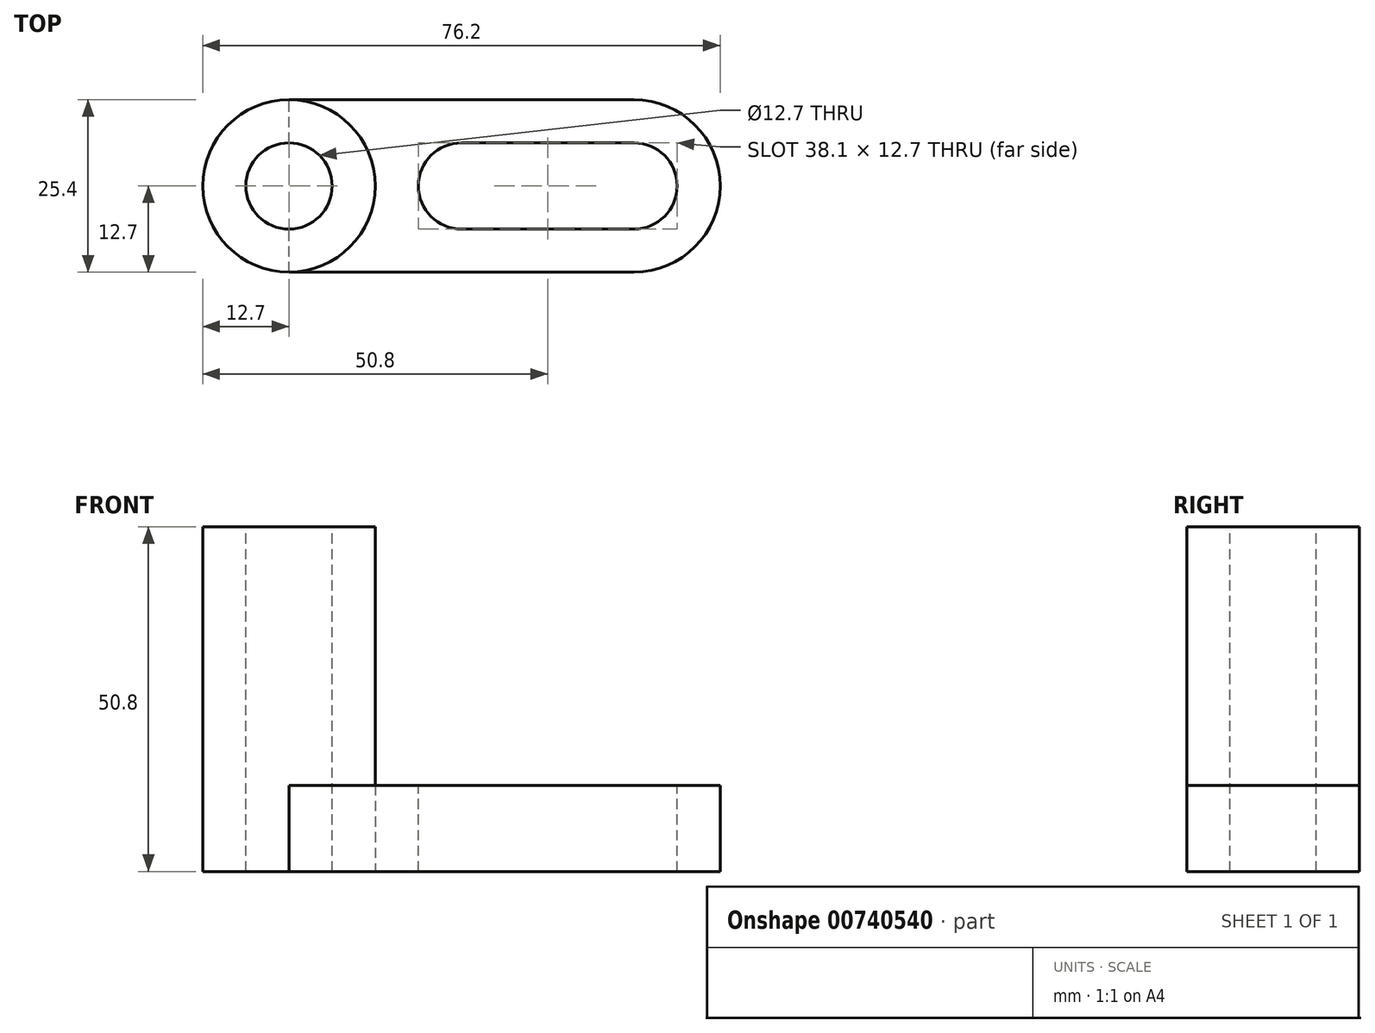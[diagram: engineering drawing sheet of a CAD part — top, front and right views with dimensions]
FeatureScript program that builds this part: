
annotation { "Feature Type Name" : "Feature", "Feature Type Description" : "" }
export const myFeature = defineFeature(function(context is Context, id is Id, definition is map)
    precondition{}
    {
        {
            var Q0;
            Q0=qCreatedBy(makeId("Top.planeOp"),FACE);
            var sketch = newSketch(context, id + "F0", { "sketchPlane" : qUnion([Q0])});
            skCircle(sketch, "E0", {"center": v(0, 0) * mm, "radius": 12.7 * mm});
            skSolve(sketch);
        }
        {
            var Q0;
            Q0=makeQuery(id+"F0.imprint","IMPRINT",FACE,{"disambiguationData":[TD([[makeQuery(id+"F0.imprint","IMPRINT",EDGE,{"derivedFrom":sQuery(id+"F0.wireOp",EDGE,"E0")}),1.0]])]});
            extrude(context, id + "F1", {"entities" : qUnion([Q0]), "depth" : 50.8 * mm, "offsetDistance" : 25.4 * mm});
        }
        {
            var Q0;
            Q0=qCreatedBy(makeId("Top.planeOp"),FACE);
            var sketch = newSketch(context, id + "F2", { "sketchPlane" : qUnion([Q0])});
            skLineSegment(sketch, "E1.bottom", {"start": v(0, -12.7) * mm, "end": v(50.8, -12.7) * mm});
            skLineSegment(sketch, "E1.top", {"start": v(0, 12.7) * mm, "end": v(50.8, 12.7) * mm});
            skLineSegment(sketch, "E1.left", {"start": v(0, -12.7) * mm, "end": v(0, 12.7) * mm});
            skLineSegment(sketch, "E1.right", {"start": v(50.8, -12.7) * mm, "end": v(50.8, 12.7) * mm});
            skCircle(sketch, "E2", {"center": v(50.8, 0) * mm, "radius": 12.7 * mm});
            skSolve(sketch);
        }
        {
            var Q0;
            Q0=makeQuery(id+"F2.imprint","IMPRINT",FACE,{"disambiguationData":[TD([[makeQuery(id+"F2.imprint","IMPRINT",EDGE,{"derivedFrom":sQuery(id+"F2.wireOp",EDGE,"E1.bottom")}),1.0]])]});
            var Q1;
            {var subQ0=sQuery(id+"F2.wireOp",EDGE,"E1.right");Q1=makeQuery(id+"F2.imprint","IMPRINT",FACE,{"disambiguationData":[TD([[makeQuery(id+"F2.imprint","IMPRINT",EDGE,{"derivedFrom":subQ0}),-1.0]])]});}
            var Q2;
            {var subQ0=sQuery(id+"F2.wireOp",EDGE,"E1.right");Q2=makeQuery(id+"F2.imprint","IMPRINT",FACE,{"disambiguationData":[TD([[makeQuery(id+"F2.imprint","IMPRINT",EDGE,{"derivedFrom":subQ0}),1.0]])]});}
            extrude(context, id + "F3", {"entities" : qUnion([Q0, Q1, Q2]), "depth" : 12.7 * mm, "offsetDistance" : 25.4 * mm});
        }
        {
            var Q0;
            Q0=makeQuery(id+"F3.opExtrude","CAP_FACE",FACE,{"disambiguationData":[OSD([sQuery(id+"F2.wireOp",EDGE,"E1.bottom"),sQuery(id+"F2.wireOp",EDGE,"E1.top"),sQuery(id+"F2.wireOp",EDGE,"E1.left"),sQuery(id+"F2.wireOp",EDGE,"E2")])],"isStart":false});
            var sketch = newSketch(context, id + "F4", { "sketchPlane" : qUnion([Q0])});
            skLineSegment(sketch, "E3.bottom", {"start": v(50.8, 6.35) * mm, "end": v(25.4, 6.35) * mm});
            skLineSegment(sketch, "E3.top", {"start": v(50.8, -6.35) * mm, "end": v(25.4, -6.35) * mm});
            skLineSegment(sketch, "E3.left", {"start": v(50.8, 6.35) * mm, "end": v(50.8, -6.35) * mm});
            skLineSegment(sketch, "E3.right", {"start": v(25.4, 6.35) * mm, "end": v(25.4, -6.35) * mm});
            skCircle(sketch, "E4", {"center": v(50.8, 0) * mm, "radius": 6.35 * mm});
            skCircle(sketch, "E5", {"center": v(25.4, 0) * mm, "radius": 6.35 * mm});
            skSolve(sketch);
        }
        {
            var Q0;
            {var subQ0=sQuery(id+"F4.wireOp",EDGE,"E3.left");Q0=makeQuery(id+"F4.imprint","IMPRINT",FACE,{"disambiguationData":[TD([[makeQuery(id+"F4.imprint","IMPRINT",EDGE,{"derivedFrom":subQ0}),1.0]])]});}
            var Q1;
            {var subQ0=sQuery(id+"F4.wireOp",EDGE,"E3.left");Q1=makeQuery(id+"F4.imprint","IMPRINT",FACE,{"disambiguationData":[TD([[makeQuery(id+"F4.imprint","IMPRINT",EDGE,{"derivedFrom":subQ0}),-1.0]])]});}
            var Q2;
            {var subQ0=sQuery(id+"F4.wireOp",EDGE,"E3.bottom");Q2=makeQuery(id+"F4.imprint","IMPRINT",FACE,{"disambiguationData":[TD([[makeQuery(id+"F4.imprint","IMPRINT",EDGE,{"derivedFrom":subQ0}),1.0]])]});}
            var Q3;
            {var subQ0=sQuery(id+"F4.wireOp",EDGE,"E3.right");Q3=makeQuery(id+"F4.imprint","IMPRINT",FACE,{"disambiguationData":[TD([[makeQuery(id+"F4.imprint","IMPRINT",EDGE,{"derivedFrom":subQ0}),1.0]])]});}
            var Q4;
            {var subQ0=sQuery(id+"F4.wireOp",EDGE,"E3.right");Q4=makeQuery(id+"F4.imprint","IMPRINT",FACE,{"disambiguationData":[TD([[makeQuery(id+"F4.imprint","IMPRINT",EDGE,{"derivedFrom":subQ0}),-1.0]])]});}
            extrude(context, id + "F5", {"entities" : qUnion([Q0, Q1, Q2, Q3, Q4]), "operationType" : NewBodyOperationType.REMOVE, "oppositeDirection" : true, "depth" : 12.7 * mm, "offsetDistance" : 25.4 * mm});
        }
        {
            var Q0;
            Q0=makeQuery(id+"F1.opExtrude","CAP_FACE",FACE,{"disambiguationData":[OSD([sQuery(id+"F0.wireOp",EDGE,"E0")])],"isStart":false});
            var sketch = newSketch(context, id + "F6", { "sketchPlane" : qUnion([Q0])});
            skCircle(sketch, "E6", {"center": v(0, 0) * mm, "radius": 6.35 * mm});
            skSolve(sketch);
        }
        {
            var Q0;
            Q0=makeQuery(id+"F6.imprint","IMPRINT",FACE,{"disambiguationData":[TD([[makeQuery(id+"F6.imprint","IMPRINT",EDGE,{"derivedFrom":sQuery(id+"F6.wireOp",EDGE,"E6")}),1.0]])]});
            extrude(context, id + "F7", {"entities" : qUnion([Q0]), "operationType" : NewBodyOperationType.REMOVE, "oppositeDirection" : true, "depth" : 50.8 * mm, "offsetDistance" : 25.4 * mm});
        }
        {
            var Q0;
            Q0=makeQuery(id+"F3.opExtrude","CAP_FACE",FACE,{"disambiguationData":[OSD([sQuery(id+"F2.wireOp",EDGE,"E1.bottom"),sQuery(id+"F2.wireOp",EDGE,"E1.top"),sQuery(id+"F2.wireOp",EDGE,"E1.left"),sQuery(id+"F2.wireOp",EDGE,"E2")])],"isStart":true});
            var sketch = newSketch(context, id + "F8", { "sketchPlane" : qUnion([Q0])});
            skCircle(sketch, "E7", {"center": v(0, 0) * mm, "radius": 6.35 * mm});
            skSolve(sketch);
        }
        {
            var Q0;
            {var subQ0=sQuery(id+"F8.wireOp",EDGE,"E7");var subQ1=makeQuery(id+"F3.opExtrude","CAP_EDGE",EDGE,{"disambiguationData":[OSD([sQuery(id+"F2.wireOp",EDGE,"E1.left")])],"isStart":true});var subQ2=makeQuery(id+"F8.imprint","INTERSECT",VERTEX,{"disambiguationData":[OD(0.0)],"derivedFrom":[subQ1,subQ0]});Q0=makeQuery(id+"F8.imprint","IMPRINT",FACE,{"disambiguationData":[TD([[makeQuery(id+"F8.imprint","IMPRINT",EDGE,{"disambiguationData":[TD([[subQ2,1.0]])],"derivedFrom":subQ0}),1.0]])]});}
            extrude(context, id + "F9", {"entities" : qUnion([Q0]), "operationType" : NewBodyOperationType.REMOVE, "oppositeDirection" : true, "depth" : 12.7 * mm, "offsetDistance" : 25.4 * mm});
        }
    });
